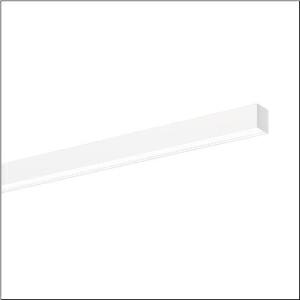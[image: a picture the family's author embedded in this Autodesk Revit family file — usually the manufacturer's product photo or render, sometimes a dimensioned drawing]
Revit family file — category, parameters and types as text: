
# Revit family: silica_r__21_51mx23da34wb_c22c
name_source: partatom
category: Lighting Fixtures
units: mm (PartAtom-declared; Revit-internal decimal feet)

## family parameters
Cut with Voids When Loaded = No
Host = Face
Light Source = No
Part Type = Normal
Room Calculation Point = No
Round Connector Dimension = Use Diameter
Shared = No

## types (1)
- --- (1 x LED, 3280 lm, 24.1 W, 3000K)
    Apparent Load = 24 VA
    CIE Flux Codes = 78 96 99 100 100
    Color Rendering = 80
    Color Temperature = 3000K
    Default Elevation = 1800 mm
    Description = Silica® 21, office luminaire, primary optical cover: prismatic diffuser, of PMMA, CAT 2 (L<= 3000cd/m²), light emission: direct distribution, primary light characteristic: symmetric, installation type: surface-mounted, LED, rated luminous flux: 3.280lm, luminous efficacy: 136lm/W, light colour: 830, colour temperature: 3000K, with terminal, 3+2-pole, max. 2.5mm², mains connection: 220..240V, AC, 50/60Hz, rated input power: 24.1W, luminaire housing, of aluminium, traffic white (RAL 9016), length: 1.204mm, width: 53mm, height: 53mm, protection rating (complete): IP20, insulation class (complete): insulation class I (protective earthing), certification: CE, permissible operating ambient temperature: 0..+35°C, standard: EN 50419, packaging unit: 1 piece
    Height = 0 mm  [stored 0 ft]
    Lamp = 1 x LED
    Lamp Light Flux = 3280 lm
    Lamp Power = 24.1 W
    Lamp count = 1
    Length = 1204 mm
    Luminous efficacy = 136 lm/W
    Manufacturer = Siteco
    ModVariant = No
    Model = 51MX23DA34WB
    Mounting Place = Ceiling
    Mounting Type = Recessed
    Number of Poles = 1
    OnlyDefault = Yes
    Power Factor = 1
    Product Name = Silica® 21
    Product group = office luminaire | ceiling recessed
    ProductGroupID = 400
    Protection Class = Protection class I
    Protection Degree = IP 20
    RLX_Detail_Level = 1
    RLX_Emergency_Light_Flux = 0 lm
    RLX_Emergency_Type = 0
    RLX_Emergency_Type_DB = No
    RlxData = <blob elided: 18845 chars, md5=7304645a>
    Socket = socket
    Standby Power = 0 W
    System Light Flux = 3280 lm
    System Power = 24 W
    Type Comments = factory setting: luminous flux: 100 % | dim-lin: 254 | 345 mA
    Type Image = l_1335877.jpg
    URL = http://relux.com
    VarID = @adj_089051
    Voltage = 0 V
    Weight = 0.00 kg
    Width = 53 mm

note: [stored X ft] marks values corroborated as IEEE doubles in the binary element streams (Revit-internal decimal feet)

## geometry (parser evidence)
native form markers: Blend x4, Sweep x9
no freeform markers — native parametric forms only
